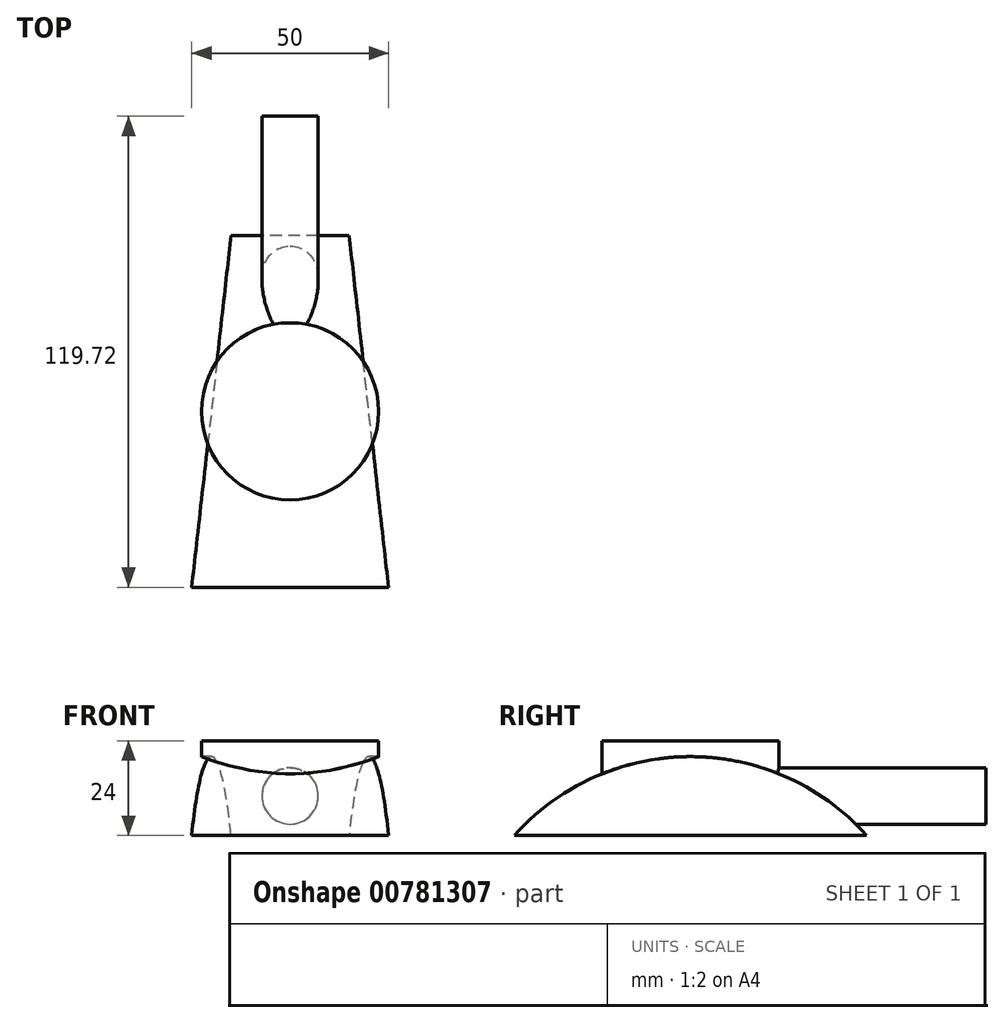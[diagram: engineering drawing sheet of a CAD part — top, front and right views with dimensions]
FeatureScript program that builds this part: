
annotation { "Feature Type Name" : "Feature", "Feature Type Description" : "" }
export const myFeature = defineFeature(function(context is Context, id is Id, definition is map)
    precondition{}
    {
        {
            var Q0;
            Q0=qCreatedBy(makeId("Top.planeOp"),FACE);
            var sketch = newSketch(context, id + "F0", { "sketchPlane" : qUnion([Q0])});
            skLineSegment(sketch, "E0", {"start": v(-15, 44.72) * mm, "end": v(-25, -44.72) * mm});
            skLineSegment(sketch, "E1", {"start": v(-25, -44.72) * mm, "end": v(25, -44.72) * mm});
            skLineSegment(sketch, "E2", {"start": v(25, -44.72) * mm, "end": v(15, 44.72) * mm});
            skLineSegment(sketch, "E3", {"start": v(15, 44.72) * mm, "end": v(-15, 44.72) * mm});
            skSolve(sketch);
        }
        {
            var Q0;
            Q0=makeQuery(id+"F0.imprint","IMPRINT",FACE,{"disambiguationData":[TD([[makeQuery(id+"F0.imprint","IMPRINT",EDGE,{"derivedFrom":sQuery(id+"F0.wireOp",EDGE,"E0")}),1.0]])]});
            extrude(context, id + "F1", {"entities" : qUnion([Q0]), "depth" : 20 * mm, "offsetDistance" : 25 * mm});
        }
        {
            var Q0;
            Q0=makeQuery(id+"F1.opExtrude","CAP_FACE",FACE,{"disambiguationData":[OSD([sQuery(id+"F0.wireOp",EDGE,"E0"),sQuery(id+"F0.wireOp",EDGE,"E1"),sQuery(id+"F0.wireOp",EDGE,"E2"),sQuery(id+"F0.wireOp",EDGE,"E3")])],"isStart":false});
            var sketch = newSketch(context, id + "F2", { "sketchPlane" : qUnion([Q0])});
            skCircle(sketch, "E4", {"center": v(0, 0) * mm, "radius": 22.5 * mm});
            skSolve(sketch);
        }
        {
            var Q0;
            Q0 = qSketchRegion(id + "F2", true);
            extrude(context, id + "F3", {"entities" : qUnion([Q0]), "operationType" : NewBodyOperationType.ADD, "depth" : 4 * mm, "offsetDistance" : 25 * mm});
        }
        {
            var Q0;
            Q0=qCreatedBy(makeId("Front.planeOp"),FACE);
            var sketch = newSketch(context, id + "F4", { "sketchPlane" : qUnion([Q0])});
            skCircle(sketch, "E5", {"center": v(0, 10) * mm, "radius": 7.16 * mm});
            skSolve(sketch);
        }
        {
            var Q0;
            Q0 = qSketchRegion(id + "F4", true);
            extrude(context, id + "F5", {"entities" : qUnion([Q0]), "operationType" : NewBodyOperationType.ADD, "oppositeDirection" : true, "depth" : 75 * mm, "offsetDistance" : 25 * mm});
        }
        {
            var Q0;
            Q0=makeQuery(id+"F1.opExtrude","CAP_EDGE",EDGE,{"disambiguationData":[OSD([sQuery(id+"F0.wireOp",EDGE,"E1")])],"isStart":false});
            var Q1;
            Q1=makeQuery(id+"F1.opExtrude","CAP_EDGE",EDGE,{"disambiguationData":[OSD([sQuery(id+"F0.wireOp",EDGE,"E3")])],"isStart":false});
            fillet(context, id + "F6", {"entities" : qUnion([Q0, Q1]), "radius" : 60 * mm, "tangentPropagation" : true, "allowEdgeOverflow" : false});
        }
    });
